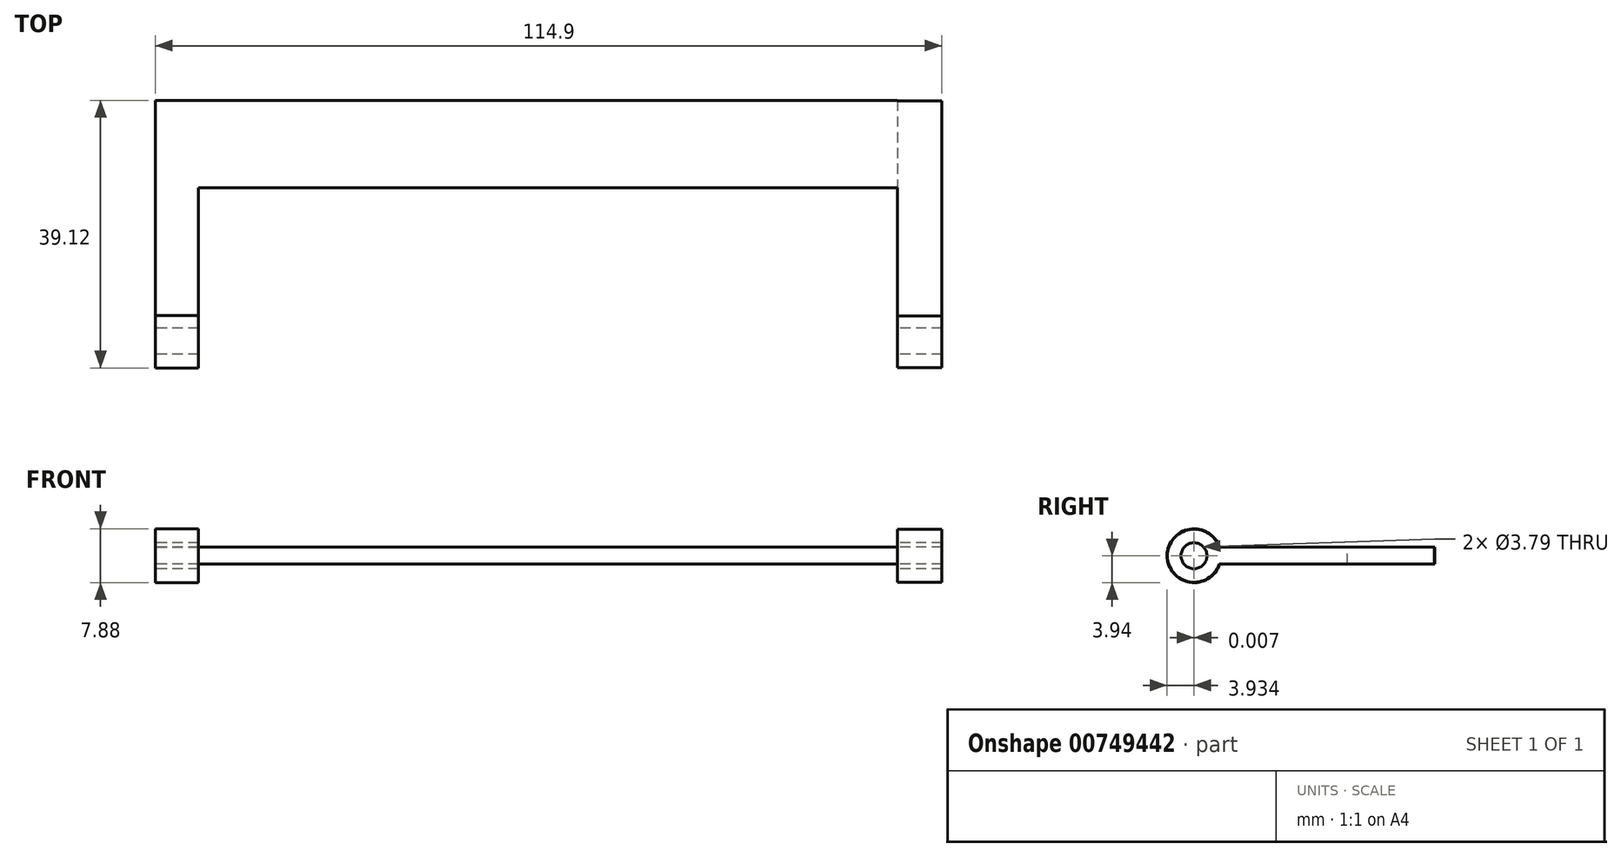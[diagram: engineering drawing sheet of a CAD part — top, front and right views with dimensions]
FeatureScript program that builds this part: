
annotation { "Feature Type Name" : "Feature", "Feature Type Description" : "" }
export const myFeature = defineFeature(function(context is Context, id is Id, definition is map)
    precondition{}
    {
        {
            var Q0;
            Q0=qCreatedBy(makeId("Right.planeOp"),FACE);
            var sketch = newSketch(context, id + "F0", { "sketchPlane" : qUnion([Q0])});
            skCircle(sketch, "E0", {"center": v(-6.16, 0) * mm, "radius": 1.9 * mm});
            skArc(sketch, "E1", {"start": v(-2.5, 1.24) * mm, "mid": v(-10.03, 0) * mm, "end": v(-2.5, -1.24) * mm});
            skLineSegment(sketch, "E2.bottom", {"start": v(28.98, -1.24) * mm, "end": v(-2.5, -1.24) * mm});
            skLineSegment(sketch, "E2.top", {"start": v(28.98, 1.24) * mm, "end": v(-2.5, 1.24) * mm});
            skLineSegment(sketch, "E2.left", {"start": v(28.98, -1.24) * mm, "end": v(28.98, 1.24) * mm});
            skPoint(sketch, "E2.middle", {"position": v(13.15, 0) * mm});
            skPoint(sketch, "E3.orphan", {"position": v(-2.68, -1.24) * mm});
            skPoint(sketch, "E4.orphan", {"position": v(-2.68, 1.24) * mm});
            skSolve(sketch);
        }
        {
            var Q0;
            Q0 = qSketchRegion(id + "F0", true);
            extrude(context, id + "F1", {"entities" : qUnion([Q0]), "depth" : 6.5 * mm, "offsetDistance" : 25 * mm});
        }
        {
            var Q0;
            Q0=qCreatedBy(makeId("Right.planeOp"),FACE);
            var sketch = newSketch(context, id + "F2", { "sketchPlane" : qUnion([Q0])});
            skLineSegment(sketch, "E5.bottom", {"start": v(29.03, -1.22) * mm, "end": v(16.24, -1.22) * mm});
            skLineSegment(sketch, "E5.top", {"start": v(29.03, 1.24) * mm, "end": v(16.24, 1.24) * mm});
            skLineSegment(sketch, "E5.left", {"start": v(29.03, -1.22) * mm, "end": v(29.03, 1.24) * mm});
            skLineSegment(sketch, "E5.right", {"start": v(16.24, -1.22) * mm, "end": v(16.24, 1.24) * mm});
            skSolve(sketch);
        }
        {
            var Q0;
            Q0 = qSketchRegion(id + "F2", true);
            extrude(context, id + "F3", {"entities" : qUnion([Q0]), "operationType" : NewBodyOperationType.ADD, "oppositeDirection" : true, "depth" : 108.4 * mm, "offsetDistance" : 25 * mm});
        }
        {
            var Q0;
            Q0=makeQuery(id+"F3.opExtrude","CAP_FACE",FACE,{"disambiguationData":[OSD([sQuery(id+"F2.wireOp",EDGE,"E5.bottom"),sQuery(id+"F2.wireOp",EDGE,"E5.top"),sQuery(id+"F2.wireOp",EDGE,"E5.left"),sQuery(id+"F2.wireOp",EDGE,"E5.right")])],"isStart":false});
            var sketch = newSketch(context, id + "F4", { "sketchPlane" : qUnion([Q0])});
            skCircle(sketch, "E6", {"center": v(6.15, 0) * mm, "radius": 1.9 * mm});
            skCircle(sketch, "E7", {"center": v(6.15, 0) * mm, "radius": 3.94 * mm});
            skLineSegment(sketch, "E8.bottom", {"start": v(-29.03, 1.24) * mm, "end": v(2.4, 1.24) * mm});
            skLineSegment(sketch, "E8.top", {"start": v(-29.03, -1.22) * mm, "end": v(2.4, -1.22) * mm});
            skLineSegment(sketch, "E8.left", {"start": v(-29.03, 1.24) * mm, "end": v(-29.03, -1.22) * mm});
            skLineSegment(sketch, "E8.right", {"start": v(2.4, 1.24) * mm, "end": v(2.4, -1.22) * mm});
            skSolve(sketch);
        }
        {
            var Q0;
            Q0 = qSketchRegion(id + "F4", true);
            extrude(context, id + "F5", {"entities" : qUnion([Q0]), "operationType" : NewBodyOperationType.ADD, "oppositeDirection" : true, "depth" : 6.3 * mm, "offsetDistance" : 25 * mm});
        }
    });
